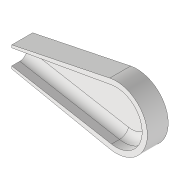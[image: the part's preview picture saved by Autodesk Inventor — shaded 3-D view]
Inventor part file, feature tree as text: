
AUTODESK INVENTOR PART (.ipt)
format: ipt  version: 2020 (Build 240168000, 168)  size: 110,080 bytes
history: native  units: mm
features: extrude x2, sketch x2, fillet x1
ambient origin geometry x8: Origin, YZ Plane, XZ Plane, XY Plane, X Axis, Y Axis, Z Axis, Center Point
bodies: Volumenkörper1 (feature_tree)
feature tree (5):
  extrude  "Extrusion1"  Depth=60.0mm
  extrude  "Extrusion2"  Depth=40.0mm TaperAngle=0.0deg
  fillet  "Rundung1"  Radius=15.0mm
  sketch  "Skizze1"  dims[d0=60.0mm d1=150.0mm]
  sketch  "Skizze2"  dims[d2=20.0mm d3=40.0mm d4=0.0mm d5=15.0mm d6=25.0mm d7=35.0mm d8=0.0mm d9=7.3mm]
